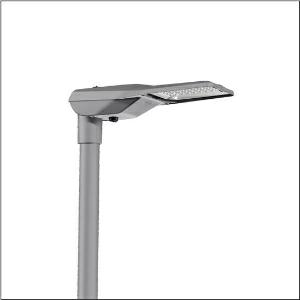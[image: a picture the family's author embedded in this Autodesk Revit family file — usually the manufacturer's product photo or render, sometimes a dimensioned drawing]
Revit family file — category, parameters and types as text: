
# Revit family: streetlight_sl_21_iq_mini___p0_5a_5xe2v31y08gb_32b4
name_source: partatom
category: Lighting Fixtures
units: mm (PartAtom-declared; Revit-internal decimal feet)

## family parameters
Cut with Voids When Loaded = No
Host = Face
Light Source = No
Part Type = Normal
Room Calculation Point = No
Round Connector Dimension = Use Diameter
Shared = No

## types (1)
- --- (1 x LED, 5880 lm, 39.8 W, 3000K)
    Apparent Load = 40 VA
    CIE Flux Codes = 37 73 96 100 100
    Color Rendering = 70
    Color Temperature = 3000K
    Default Elevation = 1800 mm
    Description = Streetlight SL 21 iQ mini, mast luminaire, primary light control with lens, of PMMA, primary optical cover: cover, of toughened safety glass, transparent, light distribution: P0.5a, light emission: direct distribution, primary light characteristic: asymmetric, installation type: post-top, side-entry, LED, High Power LED, rated luminous flux: 5.880lm, luminous efficacy: 148lm/W, light colour: 730, colour temperature: 3000K, control gear: iQ-Street Remote, D4i with power reduction, control: pre-setting: logarithmic dimming characteristic, Street-Remote, Auto-Match, Temp-Guard, Lumen-Switch, Night-Set, Smart-Wire, Light-Fading, Desk-Remote (wireless, voltage-free reading and setting of iQ features in the workshop via application-optimized NFC function/RFID function), optimised constant luminous flux control (CLO 2.0), mains connection: 220..240V, AC, 50/60Hz, start of lifetime: 40W, end of service life: 41W, reduction: 18W, luminaire housing, of diecast aluminium, powder-coated, SITECO metallic grey (DB 702S), corrosivity category C5 high according to DIN EN ISO 12944, please order mast flange separately, inclination adjustable: 0°, 5°, 10°, 15°, sealing non-destructively replaceable, multi-level sealing system, length: 628mm, width: 235mm, height: 110mm, mast flange for spigot size: 42mm (side-entry): 5XC10008XM4, 60/48mm (side-entry/post-top): 5XC10108XM2, 76/60mm (side-entry/post-top): 5XC10108XM1, mounting height: 4..8m, Smart Interface below and above, protection rating (complete): IP66, insulation class (complete): insulation class II (safety insulation), certification: CE, ENEC, ENEC+, VDE, impact resistance: IK10, permissible operating ambient temperature for outdoor applications: -40..+50°C, standard-compliant lighting for roads and squares, packaging unit: 1 piece

Light Distribution: P0.5a
    Height = 110 mm
    Lamp = 1 x LED
    Lamp Light Flux = 5880 lm
    Lamp Power = 39.8 W
    Lamp count = 1
    Length = 625 mm
    Luminous efficacy = 148 lm/W
    Manufacturer = Siteco
    ModVariant = No
    Model = 5XE2V31Y08GB
    Mounting Place = Pole
    Mounting Type = Pole top
    Number of Poles = 1
    OnlyDefault = Yes
    Power Factor = 1
    Product Name = Streetlight SL 21 iQ mini | P0.5a
    Product group = mast luminaire | pylon top
    ProductGroupID = 6100
    Protection Class = Protection class II
    Protection Degree = IP 66
    RLX_Detail_Level = 1
    RLX_Emergency_Light_Flux = 0 lm
    RLX_Emergency_Type = 0
    RLX_Emergency_Type_DB = No
    RlxData = <blob elided: 92177 chars, md5=d2ae7fd2>
    Socket = socket
    Standby Power = 0 W
    System Light Flux = 5880 lm
    System Power = 40 W
    Type Comments = factory setting: luminous flux: 100 % | dim-lin: 254 | 800 mA
    Type Image = l_1003514.jpg
    URL = http://relux.com
    VarID = @adj_079897
    Voltage = 0 V
    Weight = 0.00 kg
    Width = 234 mm

## geometry (parser evidence)
native form markers: Blend x4, Sweep x11
no freeform markers — native parametric forms only
